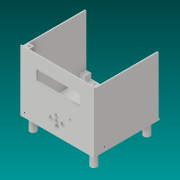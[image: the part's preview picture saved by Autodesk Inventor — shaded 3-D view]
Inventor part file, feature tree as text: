
AUTODESK INVENTOR PART (.ipt)
format: ipt  version: 2019 (Build 230136000, 136)  size: 1,059,840 bytes
history: native  units: mm
features: sketch x31, extrude x18, delete_face x8, other x8, hole x6, fillet x4, boolean_combine x1
ambient origin geometry x8: Origin, YZ Plane, XZ Plane, XY Plane, X Axis, Y Axis, Z Axis, Center Point
bodies: Solid1 (feature_tree), Solid2 (feature_tree), Solid3 (feature_tree), Solid4 (feature_tree), Solid5 (feature_tree), Solid6 (feature_tree), Solid137 (feature_tree), Solid139 (feature_tree), Solid141 (feature_tree), Solid142 (feature_tree)
feature tree (76):
  extrude  "Extrusion1"  Depth=5.0mm
  fillet  "Fillet1"  Radius=5.0mm
  delete_face  "Delete Face1"
  delete_face  "Delete Face2"
  delete_face  "Delete Face3"
  delete_face  "Delete Face4"
  delete_face  "Delete Face5"
  sketch  "Sketch2"  dims[d3=5.0mm d4=5.0mm]
  sketch  "Sketch3"  dims[d5=2.5mm d12=2.0mm d13=0.0mm d14=0.5mm]
  extrude  "Extrusion2"  Depth=5.0mm
  hole  "Hole1"  [1 undecoded]
  boolean_combine  "Combine1"
  fillet  "Fillet2"  Radius=0.5mm
  extrude  "Extrusion3"  Depth=2.0mm
  extrude  "Extrusion4"  TaperAngle=0.0deg  [1 undecoded]
  sketch  "Sketch8"  dims[d31=2.1mm d32=2.0mm]
  sketch  "Sketch9"  dims[d33=2.0mm d34=0.0mm d35=100.0mm]
  extrude  "Extrusion5"  Depth=2.0mm
  extrude  "Extrusion6"  Depth=2.0mm TaperAngle=0.0deg
  extrude  "Extrusion7"  Depth=2.0mm
  extrude  "Extrusion8"  Depth=100.0mm
  extrude  "Extrusion9"  Depth=2.0mm
  extrude  "Extrusion10"  Depth=2.0mm TaperAngle=0.0deg
  hole  "Hole2"  [1 undecoded]
  delete_face  "Delete Face6"
  delete_face  "Delete Face7"
  delete_face  "Delete Face39"
  sketch  "Sketch17"  dims[d63=3.2mm d64=6.0mm d65=4.0mm d66=2.0mm d67=90.0deg d68=4.0mm d69=0.0mm d70=10.0mm]
  extrude  "Extrusion11"  Depth=10.0mm
  hole  "Hole3"  [1 undecoded]
  extrude  "Extrusion12"  Depth=10.0mm
  extrude  "Extrusion13"  Depth=10.0mm TaperAngle=0.0deg
  hole  "Hole4"  [1 undecoded]
  hole  "Hole5"  [1 undecoded]
  extrude  "Extrusion14"  Depth=10.0mm
  sketch  "Sketch25"  dims[d109=9.5mm d110=9.5mm]
  extrude  "Extrusion15"  Depth=8.0mm
  fillet  "Fillet3"  Radius=1.5mm
  hole  "Hole6"  [1 undecoded]
  sketch  "Sketch28"  dims[d116=5.5mm]
  extrude  "Extrusion16"  Depth=10.0mm
  extrude  "Extrusion17"  Depth=9.5mm
  extrude  "Extrusion18"  Depth=2.0mm
  fillet  "Fillet4"  Radius=5.5mm
  sketch  "Sketch1"  dims[d0=5.0mm d1=5.0mm d2=5.0mm]
  sketch  "Sketch4"  dims[d15=2.0mm d16=2.0mm]
  sketch  "Sketch5"  dims[d17=2.0mm d18=0.0mm d19=0.0mm]
  sketch  "Sketch6"  dims[d20=3.2mm d21=6.0mm d22=4.0mm d23=2.0mm d24=90.0deg d25=4.0mm d26=0.0mm d27=2.0mm]
  sketch  "Sketch7"  dims[d28=2.0mm d29=2.0mm d30=0.0mm]
  sketch  "Sketch10"  dims[d36=2.0mm d37=0.0mm d38=2.0mm]
  sketch  "Sketch11"  dims[d39=2.0mm d40=2.0mm d41=0.0mm]
  sketch  "Sketch12"  dims[d42=2.0mm d43=0.0mm d44=2.0mm d45=0.0mm]
  sketch  "Sketch13"  dims[d46=10.0mm d47=10.0mm]
  sketch  "Sketch14"  dims[d48=10.0mm d49=0.0mm d50=2.0mm d51=0.0mm]
  sketch  "Sketch15"  dims[d52=3.2mm d53=6.0mm d54=4.0mm d55=2.0mm d56=90.0deg d57=4.0mm d58=0.0mm d59=10.0mm]
  sketch  "Sketch16"  dims[d60=10.0mm d61=10.0mm d62=0.0mm]
  sketch  "Sketch18"  dims[d71=10.0mm d72=10.0mm d73=0.0mm]
  sketch  "Sketch19"  dims[d74=10.0mm d75=10.0mm]
  sketch  "Sketch20"  dims[d76=10.0mm d77=0.0mm]
  sketch  "Sketch21"  dims[d78=3.2mm d79=6.0mm d80=4.0mm d81=2.0mm d82=90.0deg d83=4.0mm d84=0.0mm d85=8.0mm]
  sketch  "Sketch22"  dims[d86=3.2mm d87=6.0mm d88=4.0mm d89=2.0mm d90=90.0deg d91=4.0mm d92=0.0mm d97=1.5mm]
  sketch  "Sketch23"  dims[d100=5.0mm d105=5.0mm]
  sketch  "Sketch24"  dims[d106=10.0mm d107=0.0mm d108=9.5mm]
  sketch  "Sketch26"  dims[d111=10.0mm d112=0.0mm d113=2.0mm d114=5.5mm]
  sketch  "Sketch27"  dims[d115=5.5mm]
  sketch  "Sketch29"  dims[d117=3.2mm d118=6.0mm d119=4.0mm d120=2.0mm d121=90.0deg d122=4.0mm d123=0.0mm]
  sketch  "Sketch30"  dims[d143=10.0mm d144=0.0mm]
  sketch  "Sketch31"  dims[d145=10.0mm d146=0.0mm d149=10.0mm d152=10.0mm d158=10.0mm d159=20.0mm d160=0.0mm d161=2.0mm]
  other  "Open CASCADE STEP translator 6.8 1.1.1_1:1"
  other  "4301x60507x6_3:1"
  other  "4301x60507x6_5:1"
  other  "4301x60507x6_7:1"
  other  "4301x60507x6_9:1"
  other  "4301x60507x6_11:1"
  other  "RC1602B-BIW-CSV--3DModel-STEP-56544_70:28"
  other  "RC1602B-BIW-CSV--3DModel-STEP-56544_70:30"
note: 7 required parameter values undecoded (feature->parameter linkage not recoverable at this tier; creation-order binding heuristic only, values carry confidence <= 0.55)
